# Revit family: Carport
name_source: partatom
category: Structural Framing
revit_build: Autodesk Revit 2018 (Build: 20170223_1515(x64)
units: mm (PartAtom-declared; Revit-internal decimal feet)

## family parameters
Always export as geometry = No
Always vertical = Yes
Cut with Voids When Loaded = No
Material for Model Behavior = Other
Section Shape = Not Defined
Shared = No
Show family pre-cut in plan views = No
Structural Framing Length Roundoff = 0' - 0"
Work Plane-Based = No

## types (4) — shared parameters
Array Margin = 10' - 0"
Channel Height = 1' - 0"
Channel Radius = 0' - 0 3/4"
Channel Return = 0' - 2"
Channel Width = 0' - 2"
Channel thickness = 0' - 0 1/4"
Half of Loop Depth = 7' - 0"
Height = 0' - 5 1/2"
Length = 4' - 6"
Loop Depth = 14' - 0"
MAterial = Trellis BM Runyon Canyon
Width = 0' - 5 1/2"

## per-type parameters (varying)
| type | Array Count | Array Length | Array Spaces | Deck Visibility | Loop Length | Post Height | Tilt |
| Carport | 2 | 20' - 0" | 1 | No | 40' - 0" | 9' - 6" | 15.00° |
| Carport 3 | 2 | 9' - 8" | 1 | No | 29' - 8" | 9' - 6" | 2.00° |
| Carport 2 | 2 | 27' - 8" | 1 | Yes | 47' - 8" | 9' - 0" | 2.00° |
| Carport 4 | 3 | 40' - 0" | 2 | No | 60' - 0" | 9' - 6" | 2.00° |

## geometry (parser evidence)
native form markers: Blend x6, Sweep x45
no freeform markers — native parametric forms only
